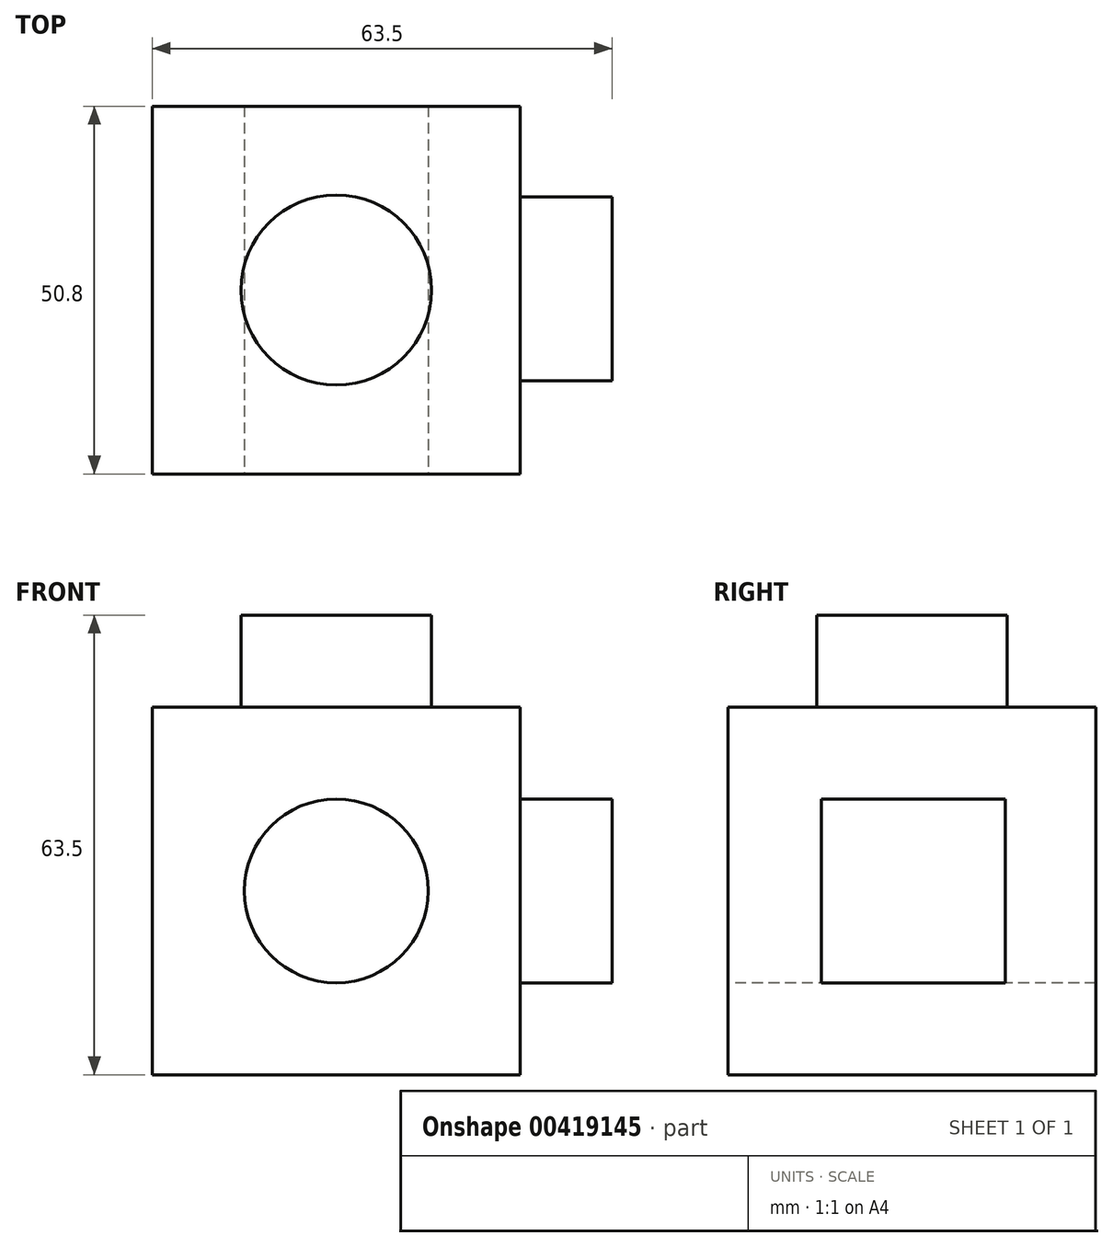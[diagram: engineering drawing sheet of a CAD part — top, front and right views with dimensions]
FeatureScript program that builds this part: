
annotation { "Feature Type Name" : "Feature", "Feature Type Description" : "" }
export const myFeature = defineFeature(function(context is Context, id is Id, definition is map)
    precondition{}
    {
        {
            var Q0;
            Q0=qCreatedBy(makeId("Front.planeOp"),FACE);
            var sketch = newSketch(context, id + "F0", { "sketchPlane" : qUnion([Q0])});
            skLineSegment(sketch, "E0", {"start": v(0, 0) * mm, "end": v(-50.8, 0) * mm});
            skLineSegment(sketch, "E1", {"start": v(-50.8, 0) * mm, "end": v(-50.8, 50.8) * mm});
            skLineSegment(sketch, "E2", {"start": v(-50.8, 50.8) * mm, "end": v(0, 50.8) * mm});
            skLineSegment(sketch, "E3", {"start": v(0, 50.8) * mm, "end": v(0, 0) * mm});
            skSolve(sketch);
        }
        {
            var Q0;
            Q0 = qSketchRegion(id + "F0", true);
            extrude(context, id + "F1", {"entities" : qUnion([Q0]), "depth" : 50.8 * mm});
        }
        {
            var Q0;
            Q0=makeQuery(id+"F1.opExtrude","CAP_FACE",FACE,{"disambiguationData":[OSD([sQuery(id+"F0.wireOp",EDGE,"E0"),sQuery(id+"F0.wireOp",EDGE,"E1"),sQuery(id+"F0.wireOp",EDGE,"E2"),sQuery(id+"F0.wireOp",EDGE,"E3")])],"isStart":false});
            var sketch = newSketch(context, id + "F2", { "sketchPlane" : qUnion([Q0])});
            skCircle(sketch, "E4", {"center": v(-25.4, 25.4) * mm, "radius": 12.7 * mm});
            skSolve(sketch);
        }
        {
            var Q0;
            Q0 = qSketchRegion(id + "F2", true);
            extrude(context, id + "F3", {"entities" : qUnion([Q0]), "operationType" : NewBodyOperationType.REMOVE, "oppositeDirection" : true, "depth" : 50.8 * mm});
        }
        {
            var Q0;
            Q0=qCreatedBy(makeId("Right.planeOp"),FACE);
            var sketch = newSketch(context, id + "F4", { "sketchPlane" : qUnion([Q0])});
            skLineSegment(sketch, "E5.bottom", {"start": v(-37.92, 38.1) * mm, "end": v(-12.52, 38.1) * mm});
            skLineSegment(sketch, "E5.top", {"start": v(-37.92, 12.7) * mm, "end": v(-12.52, 12.7) * mm});
            skLineSegment(sketch, "E5.left", {"start": v(-37.92, 38.1) * mm, "end": v(-37.92, 12.7) * mm});
            skLineSegment(sketch, "E5.right", {"start": v(-12.52, 38.1) * mm, "end": v(-12.52, 12.7) * mm});
            skSolve(sketch);
        }
        {
            var Q0;
            Q0 = qSketchRegion(id + "F4", true);
            extrude(context, id + "F5", {"entities" : qUnion([Q0]), "operationType" : NewBodyOperationType.ADD, "depth" : 12.7 * mm});
        }
        {
            var Q0;
            Q0=makeQuery(id+"F1.opExtrude","SWEPT_FACE",FACE,{"disambiguationData":[OSD([sQuery(id+"F0.wireOp",EDGE,"E2")])]});
            var sketch = newSketch(context, id + "F6", { "sketchPlane" : qUnion([Q0])});
            skCircle(sketch, "E6", {"center": v(-25.4, -25.4) * mm, "radius": 13.14 * mm});
            skSolve(sketch);
        }
        {
            var Q0;
            Q0 = qSketchRegion(id + "F6", true);
            extrude(context, id + "F7", {"entities" : qUnion([Q0]), "operationType" : NewBodyOperationType.ADD, "depth" : 12.7 * mm});
        }
    });
